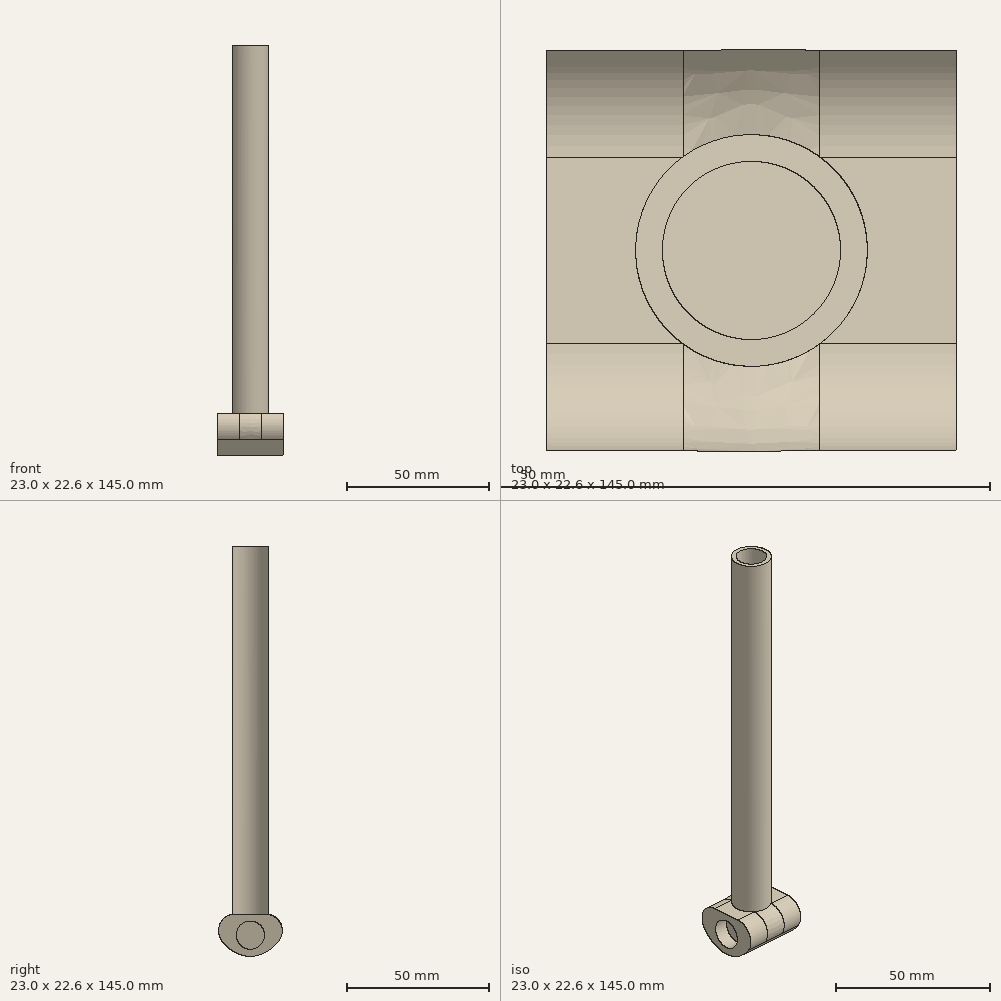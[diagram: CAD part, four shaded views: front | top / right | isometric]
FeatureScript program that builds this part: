
annotation { "Feature Type Name" : "Feature", "Feature Type Description" : "" }
export const myFeature = defineFeature(function(context is Context, id is Id, definition is map)
    precondition{}
    {
        {
            var Q0;
            Q0=qCreatedBy(makeId("Top.planeOp"),FACE);
            var sketch = newSketch(context, id + "F0", { "sketchPlane" : qUnion([Q0])});
            skLineSegment(sketch, "E0.bottom", {"start": v(-11.5, 12.5) * mm, "end": v(11.5, 12.5) * mm});
            skLineSegment(sketch, "E0.top", {"start": v(-11.5, -12.5) * mm, "end": v(11.5, -12.5) * mm});
            skLineSegment(sketch, "E0.left", {"start": v(-11.5, 12.5) * mm, "end": v(-11.5, -12.5) * mm});
            skLineSegment(sketch, "E0.right", {"start": v(11.5, 12.5) * mm, "end": v(11.5, -12.5) * mm});
            skPoint(sketch, "E0.middle", {"position": v(0, 0) * mm});
            skSolve(sketch);
        }
        {
            var Q0;
            Q0 = qSketchRegion(id + "F0", true);
            extrude(context, id + "F1", {"entities" : qUnion([Q0]), "depth" : 15 * mm});
        }
        {
            var Q0;
            Q0=makeQuery(id+"F1.opExtrude","CAP_FACE",FACE,{"disambiguationData":[OSD([sQuery(id+"F0.wireOp",EDGE,"E0.bottom"),sQuery(id+"F0.wireOp",EDGE,"E0.top"),sQuery(id+"F0.wireOp",EDGE,"E0.left"),sQuery(id+"F0.wireOp",EDGE,"E0.right")])],"isStart":false});
            var sketch = newSketch(context, id + "F2", { "sketchPlane" : qUnion([Q0])});
            skCircle(sketch, "E1", {"center": v(0, 0) * mm, "radius": 6.5 * mm});
            skSolve(sketch);
        }
        {
            var Q0;
            Q0=makeQuery(id+"F2.imprint","IMPRINT",FACE,{"disambiguationData":[TD([[makeQuery(id+"F2.imprint","IMPRINT",EDGE,{"derivedFrom":sQuery(id+"F2.wireOp",EDGE,"E1")}),1.0]])]});
            extrude(context, id + "F3", {"entities" : qUnion([Q0]), "operationType" : NewBodyOperationType.ADD, "depth" : 130 * mm});
        }
        {
            var Q0;
            Q0=makeQuery(id+"F1.opExtrude","SWEPT_FACE",FACE,{"disambiguationData":[OSD([sQuery(id+"F0.wireOp",EDGE,"E0.left")])]});
            var sketch = newSketch(context, id + "F4", { "sketchPlane" : qUnion([Q0])});
            skCircle(sketch, "E2", {"center": v(0, 7.5) * mm, "radius": 5 * mm});
            skPoint(sketch, "E2.centerSnap0", {"position": v(0, 15) * mm});
            skSolve(sketch);
        }
        {
            var Q0;
            Q0=makeQuery(id+"F4.imprint","IMPRINT",FACE,{"disambiguationData":[TD([[makeQuery(id+"F4.imprint","IMPRINT",EDGE,{"derivedFrom":sQuery(id+"F4.wireOp",EDGE,"E2")}),1.0]])]});
            extrude(context, id + "F5", {"entities" : qUnion([Q0]), "operationType" : NewBodyOperationType.REMOVE, "oppositeDirection" : true, "depth" : 5 * mm});
        }
        {
            var Q0;
            Q0=makeQuery(id+"F1.opExtrude","SWEPT_FACE",FACE,{"disambiguationData":[OSD([sQuery(id+"F0.wireOp",EDGE,"E0.right")])]});
            var sketch = newSketch(context, id + "F6", { "sketchPlane" : qUnion([Q0])});
            skCircle(sketch, "E3", {"center": v(0, 7.5) * mm, "radius": 5 * mm});
            skSolve(sketch);
        }
        {
            var Q0;
            Q0=makeQuery(id+"F6.imprint","IMPRINT",FACE,{"disambiguationData":[TD([[makeQuery(id+"F6.imprint","IMPRINT",EDGE,{"derivedFrom":sQuery(id+"F6.wireOp",EDGE,"E3")}),1.0]])]});
            extrude(context, id + "F7", {"entities" : qUnion([Q0]), "operationType" : NewBodyOperationType.REMOVE, "oppositeDirection" : true, "depth" : 5 * mm});
        }
        {
            var Q0;
            Q0=makeQuery(id+"F1.opExtrude","CAP_EDGE",EDGE,{"disambiguationData":[OSD([sQuery(id+"F0.wireOp",EDGE,"E0.bottom")])],"isStart":true});
            var Q1;
            Q1=makeQuery(id+"F1.opExtrude","CAP_EDGE",EDGE,{"disambiguationData":[OSD([sQuery(id+"F0.wireOp",EDGE,"E0.top")])],"isStart":true});
            fillet(context, id + "F8", {"entities" : qUnion([Q0, Q1]), "radius" : 13 * mm, "tangentPropagation" : true, "allowEdgeOverflow" : false});
        }
        {
            var Q0;
            Q0=makeQuery(id+"F1.opExtrude","CAP_EDGE",EDGE,{"disambiguationData":[OSD([sQuery(id+"F0.wireOp",EDGE,"E0.bottom")])],"isStart":false});
            var Q1;
            Q1=makeQuery(id+"F1.opExtrude","CAP_EDGE",EDGE,{"disambiguationData":[OSD([sQuery(id+"F0.wireOp",EDGE,"E0.top")])],"isStart":false});
            fillet(context, id + "F9", {"entities" : qUnion([Q0, Q1]), "radius" : 6 * mm, "tangentPropagation" : true, "allowEdgeOverflow" : false});
        }
        {
            var Q0;
            Q0=makeQuery(id+"F3.opExtrude","CAP_FACE",FACE,{"disambiguationData":[OSD([sQuery(id+"F2.wireOp",EDGE,"E1")])],"isStart":false});
            var sketch = newSketch(context, id + "F10", { "sketchPlane" : qUnion([Q0])});
            skCircle(sketch, "E4", {"center": v(0, 0) * mm, "radius": 5 * mm});
            skSolve(sketch);
        }
        {
            var Q0;
            Q0=makeQuery(id+"F10.imprint","IMPRINT",FACE,{"disambiguationData":[TD([[makeQuery(id+"F10.imprint","IMPRINT",EDGE,{"derivedFrom":sQuery(id+"F10.wireOp",EDGE,"E4")}),1.0]])]});
            extrude(context, id + "F11", {"entities" : qUnion([Q0]), "operationType" : NewBodyOperationType.REMOVE, "oppositeDirection" : true, "depth" : 129 * mm});
        }
    });
